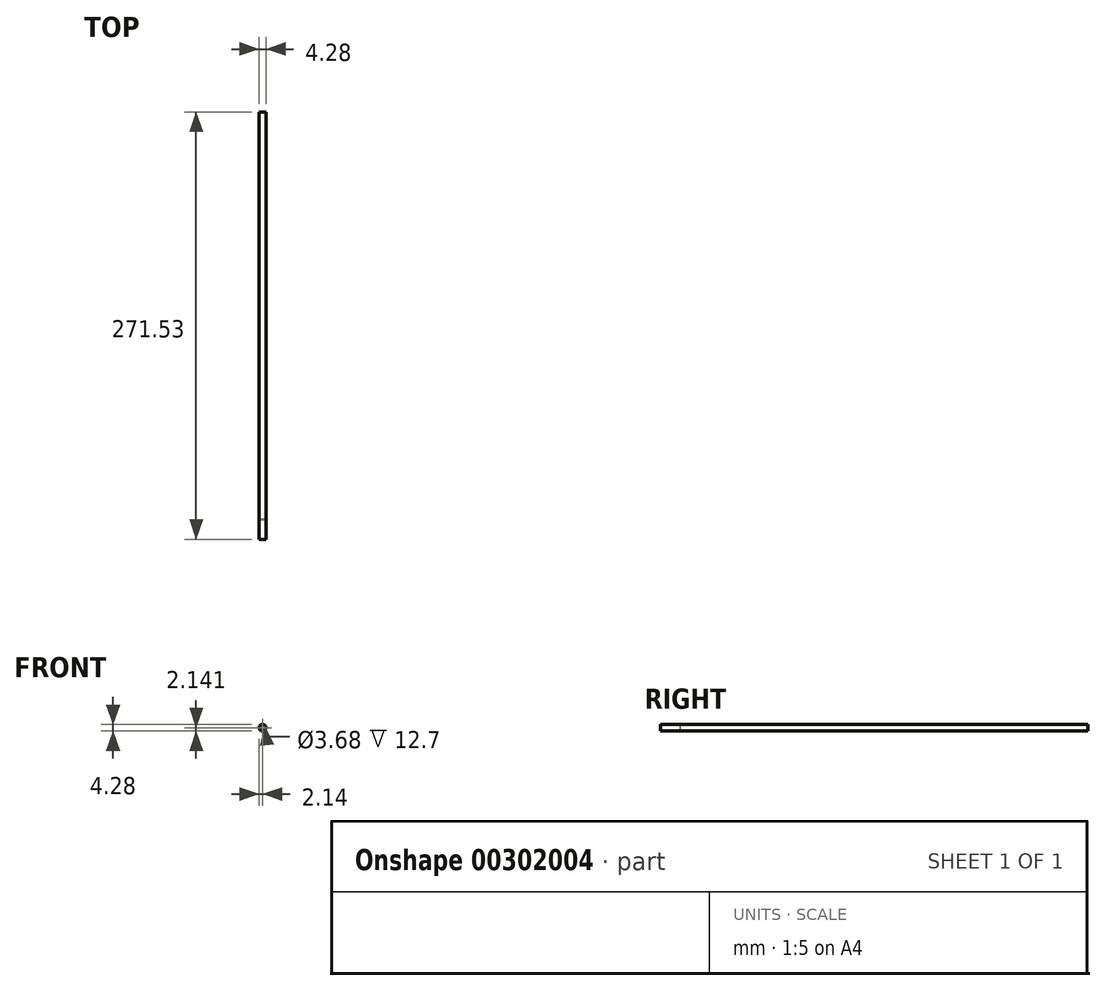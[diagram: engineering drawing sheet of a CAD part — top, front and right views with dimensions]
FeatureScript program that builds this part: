
annotation { "Feature Type Name" : "Feature", "Feature Type Description" : "" }
export const myFeature = defineFeature(function(context is Context, id is Id, definition is map)
    precondition{}
    {
        {
            var Q0;
            Q0=qCreatedBy(makeId("Front.planeOp"),FACE);
            var sketch = newSketch(context, id + "F0", { "sketchPlane" : qUnion([Q0])});
            skCircle(sketch, "E0", {"center": v(16.5, -18.32) * mm, "radius": 2.14 * mm});
            skSolve(sketch);
        }
        {
            var Q0;
            Q0=makeQuery(id+"F0.imprint","IMPRINT",FACE,{"disambiguationData":[TD([[makeQuery(id+"F0.imprint","IMPRINT",EDGE,{"derivedFrom":sQuery(id+"F0.wireOp",EDGE,"E0")}),1.0]])]});
            extrude(context, id + "F1", {"entities" : qUnion([Q0]), "depth" : 271.53 * mm});
        }
        {
            var Q0;
            Q0=makeQuery(id+"F1.opExtrude","CAP_FACE",FACE,{"disambiguationData":[OSD([sQuery(id+"F0.wireOp",EDGE,"E0")])],"isStart":false});
            var sketch = newSketch(context, id + "F2", { "sketchPlane" : qUnion([Q0])});
            skCircle(sketch, "E1", {"center": v(16.5, -18.32) * mm, "radius": 1.84 * mm});
            skCircle(sketch, "E2", {"center": v(16.5, -18.32) * mm, "radius": 2.2 * mm});
            skCircle(sketch, "E3", {"center": v(16.5, -18.32) * mm, "radius": 2.24 * mm});
            skSolve(sketch);
        }
        {
            var Q0;
            Q0=makeQuery(id+"F2.imprint","IMPRINT",FACE,{"disambiguationData":[TD([[makeQuery(id+"F2.imprint","IMPRINT",EDGE,{"derivedFrom":sQuery(id+"F2.wireOp",EDGE,"E1")}),1.0]])]});
            var Q1;
            Q1=sQuery(id+"F2.wireOp",EDGE,"E1");
            extrude(context, id + "F3", {"entities" : qUnion([Q0]), "operationType" : NewBodyOperationType.REMOVE, "surfaceEntities" : qUnion([Q1]), "oppositeDirection" : true, "depth" : 12.7 * mm});
        }
        {
            var Q0;
            Q0=sQuery(id+"F2.wireOp",EDGE,"E2");
            extrude(context, id + "F4", {"bodyType" : ToolBodyType.SURFACE, "surfaceEntities" : qUnion([Q0]), "oppositeDirection" : true, "depth" : 7.87 * mm});
        }
        {
            var Q0;
            Q0=sQuery(id+"F2.wireOp",EDGE,"E3");
            extrude(context, id + "F5", {"bodyType" : ToolBodyType.SURFACE, "surfaceEntities" : qUnion([Q0]), "oppositeDirection" : true, "depth" : 0.74 * mm});
        }
    });
